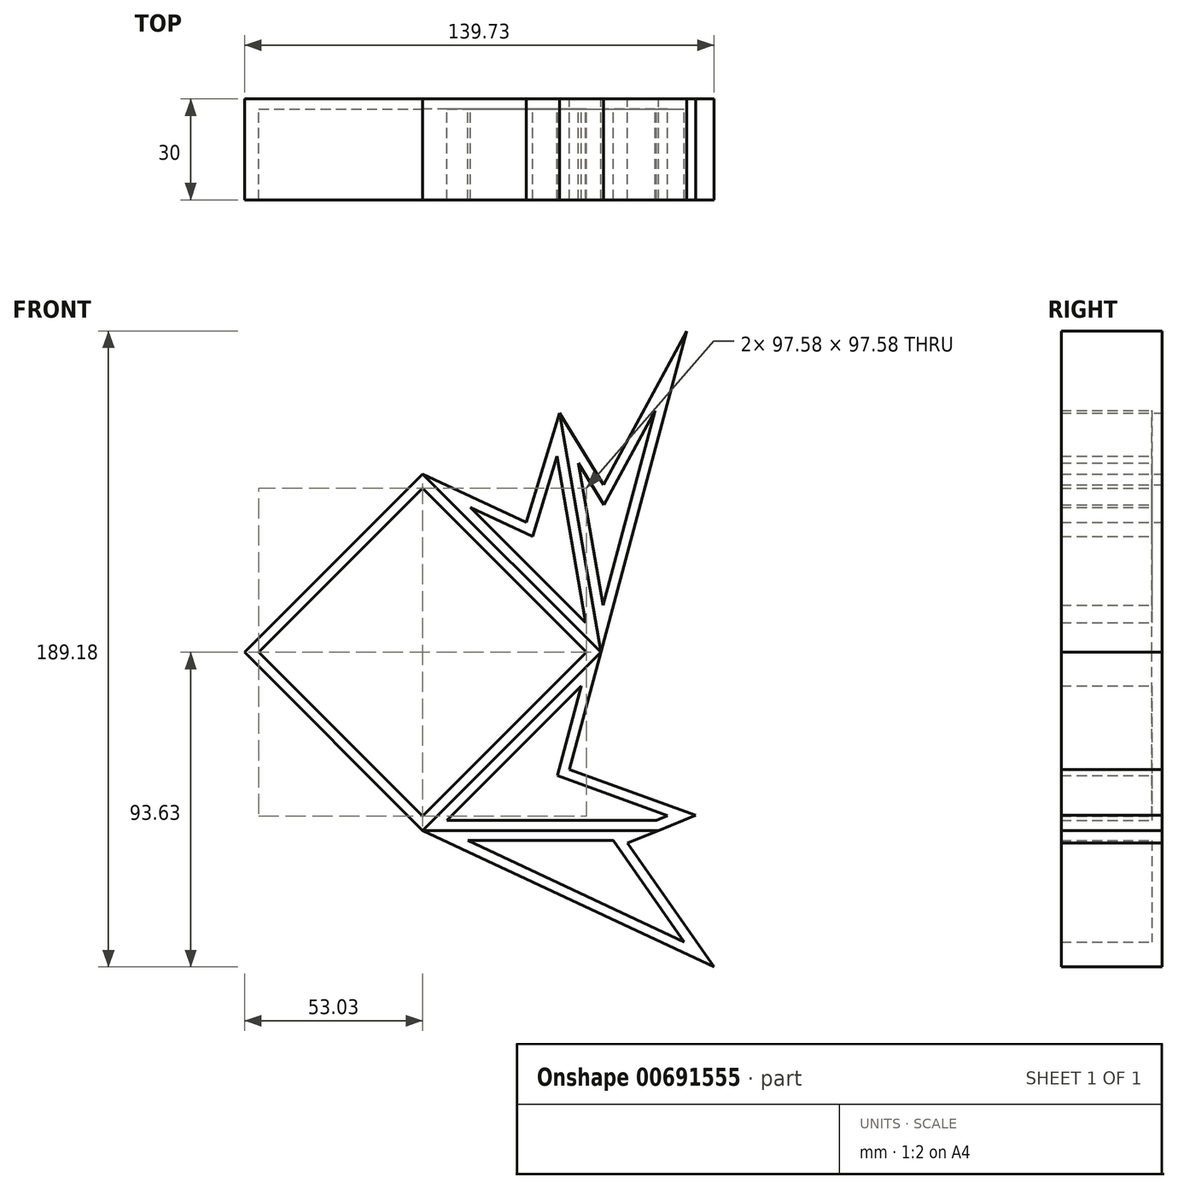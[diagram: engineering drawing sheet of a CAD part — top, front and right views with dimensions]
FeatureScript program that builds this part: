
annotation { "Feature Type Name" : "Feature", "Feature Type Description" : "" }
export const myFeature = defineFeature(function(context is Context, id is Id, definition is map)
    precondition{}
    {
        {
            var Q0;
            Q0=qCreatedBy(makeId("Front.planeOp"),FACE);
            var sketch = newSketch(context, id + "F0", { "sketchPlane" : qUnion([Q0])});
            skLineSegment(sketch, "E0", {"start": v(-53.03, 0) * mm, "end": v(0, 53.03) * mm});
            skLineSegment(sketch, "E1", {"start": v(0, 53.03) * mm, "end": v(53.03, 0) * mm});
            skLineSegment(sketch, "E2", {"start": v(53.03, 0) * mm, "end": v(0, -53.03) * mm});
            skLineSegment(sketch, "E3", {"start": v(0, -53.03) * mm, "end": v(-53.03, 0) * mm});
            skLineSegment(sketch, "E4", {"start": v(0, 53.03) * mm, "end": v(30.81, 38.66) * mm});
            skLineSegment(sketch, "E5", {"start": v(30.81, 38.66) * mm, "end": v(40.76, 71.18) * mm});
            skLineSegment(sketch, "E6", {"start": v(40.76, 71.18) * mm, "end": v(53.03, 0) * mm});
            skLineSegment(sketch, "E7", {"start": v(40.76, 71.18) * mm, "end": v(53.81, 49.86) * mm});
            skLineSegment(sketch, "E8", {"start": v(53.81, 49.86) * mm, "end": v(78.64, 95.55) * mm});
            skLineSegment(sketch, "E9", {"start": v(78.64, 95.55) * mm, "end": v(43.7, -34.85) * mm});
            skLineSegment(sketch, "E10", {"start": v(43.7, -34.85) * mm, "end": v(81.28, -48.53) * mm});
            skLineSegment(sketch, "E11", {"start": v(81.28, -48.53) * mm, "end": v(60.89, -56.77) * mm});
            skLineSegment(sketch, "E12", {"start": v(60.89, -56.77) * mm, "end": v(86.7, -93.63) * mm});
            skLineSegment(sketch, "E13", {"start": v(0, -53.03) * mm, "end": v(86.7, -93.63) * mm});
            skLineSegment(sketch, "E14", {"start": v(0, -53.03) * mm, "end": v(71.08, -53.03) * mm});
            skPoint(sketch, "E14.endSnap0", {"position": v(71.08, -52.65) * mm});
            skSolve(sketch);
        }
        {
            var Q0;
            Q0=makeQuery(id+"F0.imprint","IMPRINT",FACE,{"disambiguationData":[TD([[makeQuery(id+"F0.imprint","IMPRINT",EDGE,{"derivedFrom":sQuery(id+"F0.wireOp",EDGE,"E0")}),-1.0]])]});
            extrude(context, id + "F1", {"entities" : qUnion([Q0]), "depth" : 30 * mm, "offsetDistance" : 25 * mm});
        }
        {
            var Q0;
            Q0=makeQuery(id+"F0.imprint","IMPRINT",FACE,{"disambiguationData":[TD([[makeQuery(id+"F0.imprint","IMPRINT",EDGE,{"derivedFrom":sQuery(id+"F0.wireOp",EDGE,"E1")}),1.0]])]});
            extrude(context, id + "F2", {"entities" : qUnion([Q0]), "depth" : 30 * mm, "offsetDistance" : 25 * mm});
        }
        {
            var Q0;
            {var subQ0=sQuery(id+"F0.wireOp",EDGE,"E6");Q0=makeQuery(id+"F0.imprint","IMPRINT",FACE,{"disambiguationData":[TD([[makeQuery(id+"F0.imprint","IMPRINT",EDGE,{"derivedFrom":subQ0}),1.0]])]});}
            extrude(context, id + "F3", {"entities" : qUnion([Q0]), "depth" : 30 * mm, "offsetDistance" : 25 * mm});
        }
        {
            var Q0;
            {var subQ2=sQuery(id+"F0.wireOp",EDGE,"E2");Q0=makeQuery(id+"F0.imprint","IMPRINT",FACE,{"disambiguationData":[TD([[makeQuery(id+"F0.imprint","IMPRINT",EDGE,{"derivedFrom":subQ2}),1.0]])]});}
            extrude(context, id + "F4", {"entities" : qUnion([Q0]), "depth" : 30 * mm, "offsetDistance" : 25 * mm});
        }
        {
            var Q0;
            {var subQ0=sQuery(id+"F0.wireOp",EDGE,"E12");Q0=makeQuery(id+"F0.imprint","IMPRINT",FACE,{"disambiguationData":[TD([[makeQuery(id+"F0.imprint","IMPRINT",EDGE,{"derivedFrom":subQ0}),-1.0]])]});}
            extrude(context, id + "F5", {"entities" : qUnion([Q0]), "depth" : 30 * mm, "offsetDistance" : 25 * mm});
        }
        {
            var Q0;
            Q0=makeQuery(id+"F3.opExtrude","CAP_FACE",FACE,{"disambiguationData":[OSD([sQuery(id+"F0.wireOp",EDGE,"9pPqb08s-az9F-LyaR-5PcE-ojM6BRYw20nS"),sQuery(id+"F0.wireOp",EDGE,"3Fg1t3q9-KAHj-wvSp-p7fV-fV3Iyy8dMpVZ"),sQuery(id+"F0.wireOp",EDGE,"frVtZGgW-UtEA-Fwfk-uCwu-qP6LO46hanOl"),sQuery(id+"F0.wireOp",EDGE,"z8OrORFV-rJ53-aHeO-oeop-AwfWROx0tc8M")])],"isStart":false});
            var Q1;
            Q1=makeQuery(id+"F5.opExtrude","CAP_FACE",FACE,{"disambiguationData":[OSD([sQuery(id+"F0.wireOp",EDGE,"2tnrOQhW-9Q1s-5MoX-MzYJ-NfZmBaQnRjCu"),sQuery(id+"F0.wireOp",EDGE,"X4Wx8HjL-rqjQ-22Oe-6eJp-62IHHQN2NrHk"),sQuery(id+"F0.wireOp",EDGE,"yqgZEkUh-HXVN-oU1q-rRke-7EslHAB75OQJ"),sQuery(id+"F0.wireOp",EDGE,"ahGfcUwD-Vqwx-xHNj-khZE-n8ovR9EA143Z")])],"isStart":false});
            var Q2;
            Q2=makeQuery(id+"F5.opExtrude","CAP_FACE",FACE,{"disambiguationData":[OSD([sQuery(id+"F0.wireOp",EDGE,"E11"),sQuery(id+"F0.wireOp",EDGE,"E12"),sQuery(id+"F0.wireOp",EDGE,"E13"),sQuery(id+"F0.wireOp",EDGE,"E14")])],"isStart":false});
            var Q3;
            Q3=makeQuery(id+"F4.opExtrude","CAP_FACE",FACE,{"disambiguationData":[OSD([sQuery(id+"F0.wireOp",EDGE,"E2"),sQuery(id+"F0.wireOp",EDGE,"E9"),sQuery(id+"F0.wireOp",EDGE,"E10"),sQuery(id+"F0.wireOp",EDGE,"E11"),sQuery(id+"F0.wireOp",EDGE,"E14")])],"isStart":false});
            var Q4;
            Q4=makeQuery(id+"F1.opExtrude","CAP_FACE",FACE,{"disambiguationData":[OSD([sQuery(id+"F0.wireOp",EDGE,"E0"),sQuery(id+"F0.wireOp",EDGE,"E1"),sQuery(id+"F0.wireOp",EDGE,"E2"),sQuery(id+"F0.wireOp",EDGE,"E3")])],"isStart":false});
            var Q5;
            Q5=makeQuery(id+"F2.opExtrude","CAP_FACE",FACE,{"disambiguationData":[OSD([sQuery(id+"F0.wireOp",EDGE,"E1"),sQuery(id+"F0.wireOp",EDGE,"E4"),sQuery(id+"F0.wireOp",EDGE,"E5"),sQuery(id+"F0.wireOp",EDGE,"E6")])],"isStart":false});
            var Q6;
            Q6=makeQuery(id+"F3.opExtrude","CAP_FACE",FACE,{"disambiguationData":[OSD([sQuery(id+"F0.wireOp",EDGE,"E6"),sQuery(id+"F0.wireOp",EDGE,"E7"),sQuery(id+"F0.wireOp",EDGE,"E8"),sQuery(id+"F0.wireOp",EDGE,"E9")])],"isStart":false});
            shell(context, id + "F6", {"entities" : qUnion([Q0, Q1, Q2, Q3, Q4, Q5, Q6]), "thickness" : 3 * mm});
        }
    });
